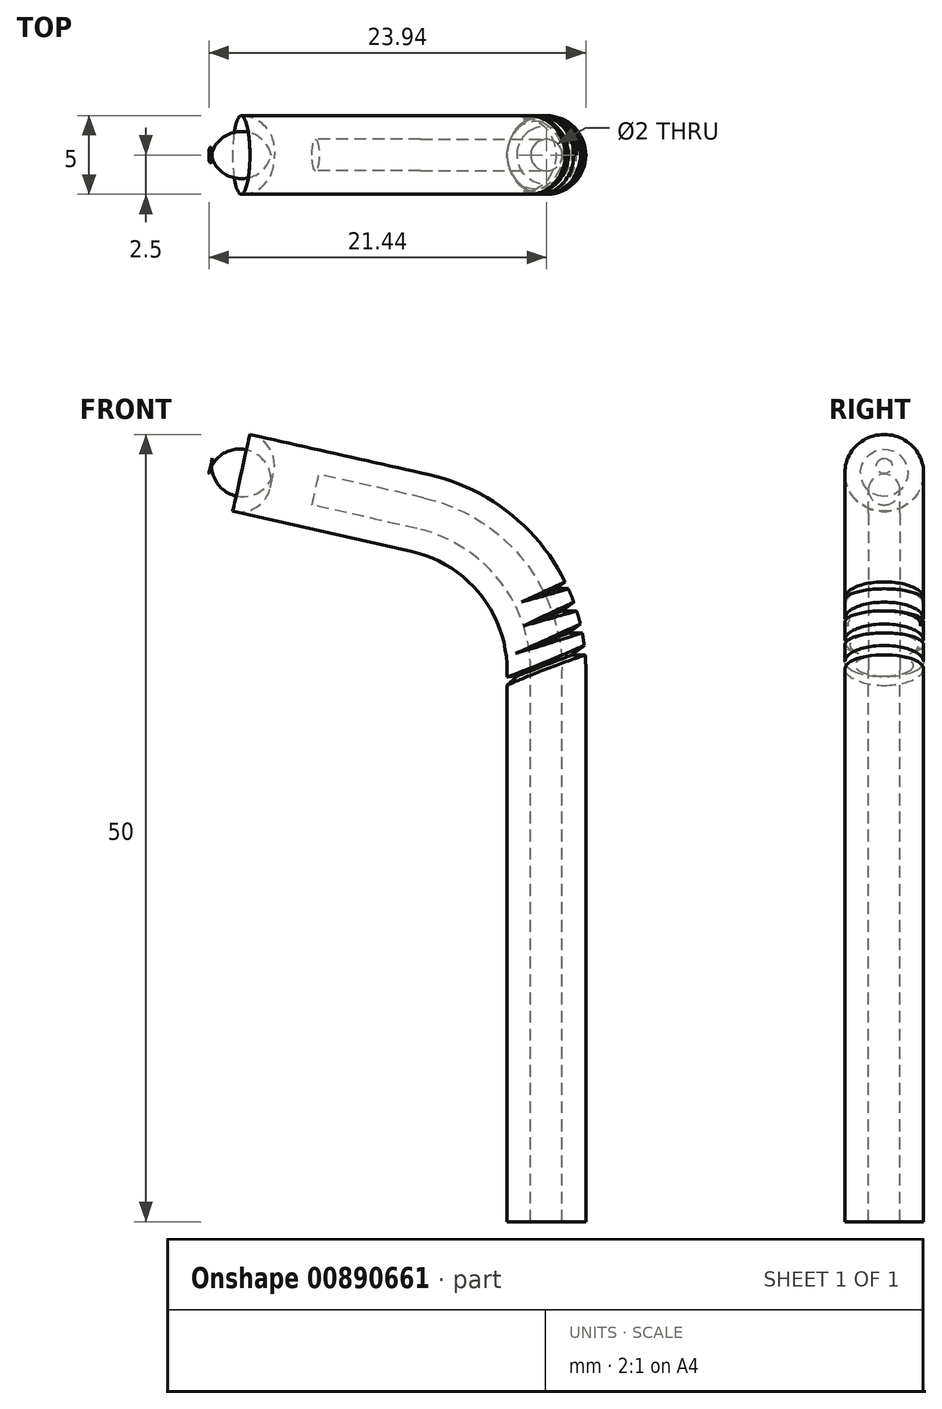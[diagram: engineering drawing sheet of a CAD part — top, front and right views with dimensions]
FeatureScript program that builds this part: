
annotation { "Feature Type Name" : "Feature", "Feature Type Description" : "" }
export const myFeature = defineFeature(function(context is Context, id is Id, definition is map)
    precondition{}
    {
        {
            var Q0;
            Q0=qCreatedBy(makeId("Front.planeOp"),FACE);
            var sketch = newSketch(context, id + "F0", { "sketchPlane" : qUnion([Q0])});
            skLineSegment(sketch, "E0", {"start": v(0, 0) * mm, "end": v(0, 35) * mm});
            skArc(sketch, "E1", {"start": v(0, 35) * mm, "mid": v(-2.25, 41.4) * mm, "end": v(-8, 45) * mm});
            skLineSegment(sketch, "E2", {"start": v(-8, 45) * mm, "end": v(-21.33, 48) * mm});
            skSolve(sketch);
        }
        {
            var Q0;
            Q0=qCreatedBy(makeId("Top.planeOp"),FACE);
            var sketch = newSketch(context, id + "F1", { "sketchPlane" : qUnion([Q0])});
            skCircle(sketch, "E3", {"center": v(0, 0) * mm, "radius": 2.5 * mm});
            skSolve(sketch);
        }
        {
            var Q0;
            Q0=makeQuery(id+"F1.imprint","IMPRINT",FACE,{"disambiguationData":[TD([[makeQuery(id+"F1.imprint","IMPRINT",EDGE,{"derivedFrom":sQuery(id+"F1.wireOp",EDGE,"E3")}),1.0]])]});
            var Q1;
            Q1=sQuery(id+"F0.wireOp",EDGE,"E0");
            var Q2;
            Q2=sQuery(id+"F0.wireOp",EDGE,"E1");
            var Q3;
            Q3=sQuery(id+"F0.wireOp",EDGE,"E2");
            sweep(context, id + "F2", {"profiles" : qUnion([Q0]), "path" : qUnion([Q1, Q2, Q3])});
        }
        {
            var Q0;
            Q0=makeQuery(id+"F2.opSweep","CAP_EDGE",EDGE,{"disambiguationData":[OSD([sQuery(id+"F0.wireOp",VERTEX,"E2.end"),sQuery(id+"F1.wireOp",EDGE,"E3")])],"isStart":false});
            fillet(context, id + "F3", {"entities" : qUnion([Q0]), "radius" : 2 * mm, "tangentPropagation" : true, "allowEdgeOverflow" : false});
        }
        {
            var Q0;
            Q0=qCreatedBy(makeId("Front.planeOp"),FACE);
            var sketch = newSketch(context, id + "F4", { "sketchPlane" : qUnion([Q0])});
            skLineSegment(sketch, "E4", {"start": v(0, 0) * mm, "end": v(0, 35) * mm});
            skArc(sketch, "E5", {"start": v(0, 35) * mm, "mid": v(-2.25, 41.4) * mm, "end": v(-8, 45) * mm});
            skLineSegment(sketch, "E6", {"start": v(-8, 45) * mm, "end": v(-14.67, 46.5) * mm});
            skSolve(sketch);
        }
        {
            var Q0;
            Q0=makeQuery(id+"F2.opSweep","CAP_FACE",FACE,{"disambiguationData":[OSD([sQuery(id+"F0.wireOp",VERTEX,"E0.start"),sQuery(id+"F1.wireOp",EDGE,"E3")])],"isStart":true});
            var sketch = newSketch(context, id + "F5", { "sketchPlane" : qUnion([Q0])});
            skCircle(sketch, "E7", {"center": v(0, 0) * mm, "radius": 1 * mm});
            skSolve(sketch);
        }
        {
            var Q0;
            Q0=makeQuery(id+"F5.imprint","IMPRINT",FACE,{"disambiguationData":[TD([[makeQuery(id+"F5.imprint","IMPRINT",EDGE,{"derivedFrom":sQuery(id+"F5.wireOp",EDGE,"E7")}),1.0]])]});
            var Q1;
            Q1=sQuery(id+"F5.wireOp",EDGE,"E7");
            var Q2;
            Q2=sQuery(id+"F4.wireOp",EDGE,"E4");
            var Q3;
            Q3=sQuery(id+"F4.wireOp",EDGE,"E5");
            var Q4;
            Q4=sQuery(id+"F4.wireOp",EDGE,"E6");
            sweep(context, id + "F6", {"operationType" : NewBodyOperationType.REMOVE, "profiles" : qUnion([Q0]), "surfaceProfiles" : qUnion([Q1]), "path" : qUnion([Q2, Q3, Q4])});
        }
        {
            var Q0;
            Q0=qCreatedBy(makeId("Front.planeOp"),FACE);
            var sketch = newSketch(context, id + "F7", { "sketchPlane" : qUnion([Q0])});
            skLineSegment(sketch, "E8", {"start": v(-3.5, 44) * mm, "end": v(0, 35) * mm});
            skSolve(sketch);
        }
        {
            var Q0;
            Q0=qCreatedBy(makeId("Front.planeOp"),FACE);
            var sketch = newSketch(context, id + "F8", { "sketchPlane" : qUnion([Q0])});
            skLineSegment(sketch, "E9", {"start": v(3.2, 36) * mm, "end": v(1.6, 36) * mm});
            skLineSegment(sketch, "E10", {"start": v(1.6, 36) * mm, "end": v(3.2, 37.2) * mm});
            skLineSegment(sketch, "E11", {"start": v(3.2, 37.2) * mm, "end": v(3.2, 36) * mm});
            skLineSegment(sketch, "E12", {"start": v(1.4, 37.4) * mm, "end": v(3, 37.4) * mm});
            skLineSegment(sketch, "E13", {"start": v(3, 37.4) * mm, "end": v(3, 38.6) * mm});
            skLineSegment(sketch, "E14", {"start": v(3, 38.6) * mm, "end": v(1.4, 37.4) * mm});
            skLineSegment(sketch, "E15", {"start": v(1, 38.8) * mm, "end": v(2.6, 38.8) * mm});
            skLineSegment(sketch, "E16", {"start": v(2.6, 38.8) * mm, "end": v(2.6, 40) * mm});
            skLineSegment(sketch, "E17", {"start": v(2.6, 40) * mm, "end": v(1, 38.8) * mm});
            skLineSegment(sketch, "E18", {"start": v(0.6, 40.2) * mm, "end": v(2.2, 40.2) * mm});
            skLineSegment(sketch, "E19", {"start": v(2.2, 41.4) * mm, "end": v(0.6, 40.2) * mm});
            skLineSegment(sketch, "E20", {"start": v(2.2, 41.4) * mm, "end": v(2.2, 40.2) * mm});
            skSolve(sketch);
        }
        {
            var Q0;
            Q0=makeQuery(id+"F8.imprint","IMPRINT",FACE,{"disambiguationData":[TD([[makeQuery(id+"F8.imprint","IMPRINT",EDGE,{"derivedFrom":sQuery(id+"F8.wireOp",EDGE,"E18")}),1.0]])]});
            var Q1;
            Q1=makeQuery(id+"F8.imprint","IMPRINT",FACE,{"disambiguationData":[TD([[makeQuery(id+"F8.imprint","IMPRINT",EDGE,{"derivedFrom":sQuery(id+"F8.wireOp",EDGE,"E15")}),1.0]])]});
            var Q2;
            Q2=makeQuery(id+"F8.imprint","IMPRINT",FACE,{"disambiguationData":[TD([[makeQuery(id+"F8.imprint","IMPRINT",EDGE,{"derivedFrom":sQuery(id+"F8.wireOp",EDGE,"E12")}),1.0]])]});
            var Q3;
            Q3=makeQuery(id+"F8.imprint","IMPRINT",FACE,{"disambiguationData":[TD([[makeQuery(id+"F8.imprint","IMPRINT",EDGE,{"derivedFrom":sQuery(id+"F8.wireOp",EDGE,"E9")}),-1.0]])]});
            var Q4;
            Q4=sQuery(id+"F7.wireOp",EDGE,"E8");
            revolve(context, id + "F9", {"operationType" : NewBodyOperationType.REMOVE, "surfaceOperationType" : NewSurfaceOperationType.NEW, "entities" : qUnion([Q0, Q1, Q2, Q3]), "axis" : qUnion([Q4]), "revolveType" : RevolveType.FULL, "oppositeDirection" : true});
        }
    });
